FCSTD DOCUMENT
Label: Components Box
objects: Sketcher::SketchObject×4
note: 4 computed .brp shape members not serialized (recipe doc carries the construction recipe); baked Part::Feature solids carry a one-line shape summary decoded from their .brp

FEATURE [Sketcher::SketchObject] Sketch001  label="side, left"
  Placement = pos=(3,0,0) rot=(0,0,1;1.5708rad)
  sketch-geometry (50):
    g0: LineSegment StartX=3 StartY=34.25 StartZ=0 EndX=3 EndY=27.9975 EndZ=0
    g1: LineSegment StartX=3 StartY=27.9975 StartZ=0 EndX=0 EndY=27.9975 EndZ=0
    g2: LineSegment StartX=0 StartY=27.9975 StartZ=0 EndX=0 EndY=21.7475 EndZ=0
    g3: LineSegment StartX=0 StartY=21.7475 StartZ=0 EndX=3 EndY=21.7475 EndZ=0
    g4: LineSegment StartX=3 StartY=21.7475 StartZ=0 EndX=3 EndY=15.4975 EndZ=0
    g5: LineSegment StartX=3 StartY=15.4975 StartZ=0 EndX=0 EndY=15.4975 EndZ=0
    g6: LineSegment StartX=0 StartY=15.4975 StartZ=0 EndX=0 EndY=9.2475 EndZ=0
    g7: LineSegment StartX=0 StartY=9.2475 StartZ=0 EndX=3 EndY=9.2475 EndZ=0
    g8: LineSegment StartX=3 StartY=9.2475 StartZ=0 EndX=3 EndY=0 EndZ=0
    g9: LineSegment StartX=3 StartY=0 StartZ=0 EndX=15.5 EndY=0 EndZ=0
    g10: LineSegment StartX=15.5 StartY=0 StartZ=0 EndX=15.5 EndY=3 EndZ=0
    g11: LineSegment StartX=15.5 StartY=3 StartZ=0 EndX=28 EndY=3 EndZ=0
    g12: LineSegment StartX=28 StartY=3 StartZ=0 EndX=28 EndY=0 EndZ=0
    g13: LineSegment StartX=28 StartY=0 StartZ=0 EndX=40.5 EndY=0 EndZ=0
    g14: LineSegment StartX=40.5 StartY=0 StartZ=0 EndX=40.5 EndY=3 EndZ=0
    g15: LineSegment StartX=40.5 StartY=3 StartZ=0 EndX=53 EndY=3 EndZ=0
    g16: LineSegment StartX=53 StartY=3 StartZ=0 EndX=53 EndY=0 EndZ=0
    g17: LineSegment StartX=53 StartY=0 StartZ=0 EndX=65.5 EndY=0 EndZ=0
    g18: LineSegment StartX=65.5 StartY=0 StartZ=0 EndX=65.5 EndY=3 EndZ=0
    g19: LineSegment StartX=65.5 StartY=3 StartZ=0 EndX=78 EndY=3 EndZ=0
    g20: LineSegment StartX=78 StartY=3 StartZ=0 EndX=78 EndY=0 EndZ=0
    g21: LineSegment StartX=78 StartY=0 StartZ=0 EndX=90.5 EndY=0 EndZ=0
    g22: LineSegment StartX=90.5 StartY=0 StartZ=0 EndX=90.5 EndY=3 EndZ=0
    g23: LineSegment StartX=90.5 StartY=3 StartZ=0 EndX=103 EndY=3 EndZ=0
    g24: LineSegment StartX=103 StartY=3 StartZ=0 EndX=103 EndY=0 EndZ=0
    g25: LineSegment StartX=103 StartY=0 StartZ=0 EndX=115.5 EndY=0 EndZ=0
    g26: LineSegment StartX=115.5 StartY=0 StartZ=0 EndX=115.5 EndY=3 EndZ=0
    g27: LineSegment StartX=115.5 StartY=3 StartZ=0 EndX=128 EndY=3 EndZ=0
    g28: LineSegment StartX=128 StartY=3 StartZ=0 EndX=128 EndY=9.25 EndZ=0
    g29: LineSegment StartX=128 StartY=9.25 StartZ=0 EndX=131 EndY=9.25 EndZ=0
    g30: LineSegment StartX=131 StartY=9.25 StartZ=0 EndX=131 EndY=15.5 EndZ=0
    g31: LineSegment StartX=131 StartY=15.5 StartZ=0 EndX=128 EndY=15.5 EndZ=0
    g32: LineSegment StartX=128 StartY=15.5 StartZ=0 EndX=128 EndY=21.75 EndZ=0
    g33: LineSegment StartX=128 StartY=21.75 StartZ=0 EndX=131 EndY=21.75 EndZ=0
    g34: LineSegment StartX=131 StartY=21.75 StartZ=0 EndX=131 EndY=28 EndZ=0
    g35: LineSegment StartX=131 StartY=28 StartZ=0 EndX=128 EndY=28 EndZ=0
    g36: LineSegment StartX=128 StartY=28 StartZ=0 EndX=128 EndY=34.25 EndZ=0
    g37: LineSegment StartX=128 StartY=34.25 StartZ=0 EndX=99 EndY=34.25 EndZ=0
    g38: LineSegment StartX=99 StartY=34.25 StartZ=0 EndX=99 EndY=18.625 EndZ=0
    g39: LineSegment StartX=99 StartY=18.625 StartZ=0 EndX=96 EndY=18.625 EndZ=0
    g40: LineSegment StartX=96 StartY=18.625 StartZ=0 EndX=96 EndY=34.25 EndZ=0
    g41: LineSegment StartX=96 StartY=34.25 StartZ=0 EndX=67 EndY=34.25 EndZ=0
    g42: LineSegment StartX=67 StartY=34.25 StartZ=0 EndX=67 EndY=18.625 EndZ=0
    g43: LineSegment StartX=67 StartY=18.625 StartZ=0 EndX=64 EndY=18.625 EndZ=0
    g44: LineSegment StartX=64 StartY=18.625 StartZ=0 EndX=64 EndY=34.25 EndZ=0
    g45: LineSegment StartX=64 StartY=34.25 StartZ=0 EndX=35 EndY=34.25 EndZ=0
    g46: LineSegment StartX=35 StartY=34.25 StartZ=0 EndX=35 EndY=18.625 EndZ=0
    g47: LineSegment StartX=35 StartY=18.625 StartZ=0 EndX=32 EndY=18.625 EndZ=0
    g48: LineSegment StartX=32 StartY=18.625 StartZ=0 EndX=32 EndY=34.25 EndZ=0
    g49: LineSegment StartX=32 StartY=34.25 StartZ=0 EndX=3 EndY=34.25 EndZ=0
  constraints (150):
    c: Coincident(g0,g1)
    c: Coincident(g1,g2)
    c: Coincident(g2,g3)
    c: Coincident(g3,g4)
    c: Coincident(g4,g5)
    c: Coincident(g5,g6)
    c: Coincident(g6,g7)
    c: Coincident(g7,g8)
    c: Coincident(g8,g9)
    c: Coincident(g9,g10)
    c: Coincident(g10,g11)
    c: Coincident(g11,g12)
    c: Coincident(g12,g13)
    c: Coincident(g13,g14)
    c: Coincident(g14,g15)
    c: Coincident(g15,g16)
    c: Coincident(g16,g17)
    c: Coincident(g17,g18)
    c: Coincident(g18,g19)
    c: Coincident(g19,g20)
    c: Coincident(g20,g21)
    c: Coincident(g21,g22)
    c: Coincident(g22,g23)
    c: Coincident(g23,g24)
    c: Coincident(g24,g25)
    c: Coincident(g25,g26)
    c: Coincident(g28,g29)
    c: Coincident(g29,g30)
    c: Coincident(g30,g31)
    c: Coincident(g31,g32)
    c: Coincident(g32,g33)
    c: Coincident(g33,g34)
    c: Coincident(g34,g35)
    c: Coincident(g35,g36)
    c: Coincident(g37,g38)
    c: Coincident(g38,g39)
    c: Coincident(g39,g40)
    c: Coincident(g40,g41)
    c: Coincident(g41,g42)
    c: Coincident(g42,g43)
    c: Coincident(g43,g44)
    c: Coincident(g44,g45)
    c: Coincident(g45,g46)
    c: Coincident(g46,g47)
    c: Coincident(g47,g48)
    c: Coincident(g48,g49)
    c: Horizontal(g49)
    c: Vertical(g48)
    c: Horizontal(g47)
    c: Vertical(g46)
    c: Horizontal(g45)
    c: Vertical(g44)
    c: Horizontal(g43)
    c: Vertical(g42)
    c: Horizontal(g41)
    c: Vertical(g40)
    c: Horizontal(g39)
    c: Vertical(g38)
    c: Horizontal(g37)
    c: Vertical(g36)
    c: Horizontal(g35)
    c: Vertical(g34)
    c: Coincident(g27,g28)
    c: Coincident(g27,g26)
    c: Vertical(g32)
    c: Vertical(g30)
    c: Vertical(g28)
    c: Vertical(g26)
    c: Horizontal(g31)
    c: Horizontal(g29)
    c: Horizontal(g27)
    c: Horizontal(g25)
    c: Horizontal(g23)
    c: Horizontal(g21)
    c: Horizontal(g19)
    c: Horizontal(g17)
    c: Horizontal(g15)
    c: Horizontal(g13)
    c: Horizontal(g11)
    c: Horizontal(g9)
    c: Horizontal(g7)
    c: Horizontal(g5)
    c: Horizontal(g1)
    c: Vertical(g24)
    c: Vertical(g22)
    c: Vertical(g20)
    c: Vertical(g18)
    c: Vertical(g16)
    c: Vertical(g14)
    c: Vertical(g12)
    c: Vertical(g10)
    c: Vertical(g8)
    c: Vertical(g6)
    c: Vertical(g4)
    c: Vertical(g2)
    c: Vertical(g0)
    c: Horizontal(g3)
    c: DistanceX(g2,g5) = 0
    c: DistanceY(g12,g9) = 0
    c: DistanceY(g14,g11) = 0
    c: DistanceX(g7,g4) = 0
    c: DistanceX(g0,g3) = 0
    c: DistanceY(g16,g13) = 0
    c: DistanceY(g18,g15) = 0
    c: DistanceY(g20,g17) = 0
    c: DistanceY(g19,g22) = 0
    c: DistanceY(g21,g24) = 0
    c: DistanceX(g28,g31) = 0
    c: DistanceX(g30,g33) = 0
    c: DistanceX(g32,g35) = 0
    c: DistanceY(g37,g40) = 0
    c: DistanceY(g39,g42) = 0
    c: DistanceY(g43,g46) = 0
    c: DistanceY(g41,g44) = 0
    c: DistanceY(g45,g48) = 0
    c: DistanceX(g41,g44) = -3
    c: DistanceX(g40,g37) = 3
    c: DistanceX(g45,g48) = -3
    c: DistanceY(g26,g23) = 0
    c: DistanceY(g26,g25) = -3
    c: DistanceX(g6,g7) = 3
    c: DistanceY(g47,g48) = 15.625
    c: DistanceX(g40,g41) = -29
    c: DistanceX(g44,g45) = -29
    c: DistanceY(g1,g2) = -6.25
    c: DistanceY(g3,g4) = -6.25
    c: DistanceY(g5,g6) = -6.25
    c: Horizontal(g33)
    c: DistanceY(g36,g35) = -6.25
    c: DistanceY(g34,g33) = -6.25
    c: DistanceY(g31,g32) = 6.25
    c: DistanceY(g29,g30) = 6.25
    c: DistanceX(g10,g11) = 12.5
    c: DistanceX(g11,g14) = 12.5
    c: DistanceX(g14,g15) = 12.5
    c: DistanceX(g17,g16) = -12.5
    c: DistanceX(g18,g19) = 12.5
    c: DistanceX(g20,g21) = 12.5
    c: DistanceX(g22,g23) = 12.5
    c: DistanceX(g24,g25) = 12.5
    c: Equal(g27,g9)
    c: Coincident(g37,g36)
    c: Coincident(g49,g0)
    c: DistanceY(g1,g0) = 6.2525
    c: DistanceX(g36,g34) = 3
    c: DistanceX(g36,g37) = -29
    c: DistanceX(g0,g48) = 29
    c: DistanceY(g27,g28) = 6.25
    c: DistanceX(g8) = 3
    c: DistanceY(g8) = 0
FEATURE [Sketcher::SketchObject] Sketch002  label="back"
  Placement = pos=(0,128,0) rot=(0,0,1;0rad)
  sketch-geometry (92):
    g0: LineSegment StartX=-0.05217 StartY=34.2293 StartZ=0 EndX=-0.05217 EndY=27.9793 EndZ=0
    g1: LineSegment StartX=-0.05217 StartY=27.9793 StartZ=0 EndX=2.94783 EndY=27.9793 EndZ=0
    g2: LineSegment StartX=2.94783 StartY=27.9793 StartZ=0 EndX=2.94783 EndY=21.7293 EndZ=0
    g3: LineSegment StartX=2.94783 StartY=21.7293 StartZ=0 EndX=-0.05217 EndY=21.7293 EndZ=0
    g4: LineSegment StartX=-0.05217 StartY=21.7293 StartZ=0 EndX=-0.05217 EndY=15.4793 EndZ=0
    g5: LineSegment StartX=-0.05217 StartY=15.4793 StartZ=0 EndX=2.94783 EndY=15.4793 EndZ=0
    g6: LineSegment StartX=2.94783 StartY=15.4793 StartZ=0 EndX=2.94783 EndY=9.2293 EndZ=0
    g7: LineSegment StartX=2.94783 StartY=9.2293 StartZ=0 EndX=-0.05217 EndY=9.2293 EndZ=0
    g8: LineSegment StartX=-0.05217 StartY=9.2293 StartZ=0 EndX=-0.05217 EndY=-0.020704 EndZ=0
    g9: LineSegment StartX=-0.05217 StartY=34.2293 StartZ=0 EndX=31.9478 EndY=34.2293 EndZ=0
    g10: LineSegment StartX=31.9478 StartY=34.2293 StartZ=0 EndX=31.9478 EndY=18.6043 EndZ=0
    g11: LineSegment StartX=31.9478 StartY=18.6043 StartZ=0 EndX=34.9478 EndY=18.6043 EndZ=0
    g12: LineSegment StartX=34.9478 StartY=18.6043 StartZ=0 EndX=34.9478 EndY=34.2293 EndZ=0
    g13: LineSegment StartX=34.9478 StartY=34.2293 StartZ=0 EndX=63.9478 EndY=34.2293 EndZ=0
    g14: LineSegment StartX=63.9478 StartY=34.2293 StartZ=0 EndX=63.9478 EndY=18.6043 EndZ=0
    g15: LineSegment StartX=63.9478 StartY=18.6043 StartZ=0 EndX=66.9478 EndY=18.6043 EndZ=0
    g16: LineSegment StartX=66.9478 StartY=18.6043 StartZ=0 EndX=66.9478 EndY=34.2293 EndZ=0
    g17: LineSegment StartX=66.9478 StartY=34.2293 StartZ=0 EndX=95.9478 EndY=34.2293 EndZ=0
    g18: LineSegment StartX=95.9478 StartY=34.2293 StartZ=0 EndX=95.9478 EndY=18.6043 EndZ=0
    g19: LineSegment StartX=95.9478 StartY=18.6043 StartZ=0 EndX=98.9478 EndY=18.6043 EndZ=0
    g20: LineSegment StartX=98.9478 StartY=18.6043 StartZ=0 EndX=98.9478 EndY=34.2293 EndZ=0
    g21: LineSegment StartX=98.9478 StartY=34.2293 StartZ=0 EndX=127.948 EndY=34.2293 EndZ=0
    g22: LineSegment StartX=127.948 StartY=34.2293 StartZ=0 EndX=127.948 EndY=18.6043 EndZ=0
    g23: LineSegment StartX=127.948 StartY=18.6043 StartZ=0 EndX=133.948 EndY=18.6043 EndZ=0
    g24: LineSegment StartX=133.948 StartY=18.6043 StartZ=0 EndX=133.948 EndY=34.2293 EndZ=0
    g25: LineSegment StartX=133.948 StartY=34.2293 StartZ=0 EndX=162.948 EndY=34.2293 EndZ=0
    g26: LineSegment StartX=162.948 StartY=34.2293 StartZ=0 EndX=162.948 EndY=18.6043 EndZ=0
    g27: LineSegment StartX=162.948 StartY=18.6043 StartZ=0 EndX=165.948 EndY=18.6043 EndZ=0
    g28: LineSegment StartX=165.948 StartY=18.6043 StartZ=0 EndX=165.948 EndY=34.2293 EndZ=0
    g29: LineSegment StartX=165.948 StartY=34.2293 StartZ=0 EndX=194.948 EndY=34.2293 EndZ=0
    g30: LineSegment StartX=194.948 StartY=34.2293 StartZ=0 EndX=194.948 EndY=18.6043 EndZ=0
    g31: LineSegment StartX=194.948 StartY=18.6043 StartZ=0 EndX=197.948 EndY=18.6043 EndZ=0
    g32: LineSegment StartX=197.948 StartY=18.6043 StartZ=0 EndX=197.948 EndY=34.2293 EndZ=0
    g33: LineSegment StartX=197.948 StartY=34.2293 StartZ=0 EndX=226.948 EndY=34.2293 EndZ=0
    g34: LineSegment StartX=226.948 StartY=34.2293 StartZ=0 EndX=226.948 EndY=18.6043 EndZ=0
    g35: LineSegment StartX=226.948 StartY=18.6043 StartZ=0 EndX=229.948 EndY=18.6043 EndZ=0
    g36: LineSegment StartX=229.948 StartY=18.6043 StartZ=0 EndX=229.948 EndY=34.2293 EndZ=0
    g37: LineSegment StartX=229.948 StartY=34.2293 StartZ=0 EndX=261.948 EndY=34.2293 EndZ=0
    g38: LineSegment StartX=261.948 StartY=34.2293 StartZ=0 EndX=261.948 EndY=27.9793 EndZ=0
    g39: LineSegment StartX=261.948 StartY=27.9793 StartZ=0 EndX=258.948 EndY=27.9793 EndZ=0
    g40: LineSegment StartX=258.948 StartY=27.9793 StartZ=0 EndX=258.948 EndY=21.7293 EndZ=0
    g41: LineSegment StartX=258.948 StartY=21.7293 StartZ=0 EndX=261.948 EndY=21.7293 EndZ=0
    g42: LineSegment StartX=261.948 StartY=21.7293 StartZ=0 EndX=261.948 EndY=15.4793 EndZ=0
    g43: LineSegment StartX=261.948 StartY=15.4793 StartZ=0 EndX=258.948 EndY=15.4793 EndZ=0
    g44: LineSegment StartX=258.948 StartY=15.4793 StartZ=0 EndX=258.948 EndY=9.2293 EndZ=0
    g45: LineSegment StartX=258.948 StartY=9.2293 StartZ=0 EndX=261.948 EndY=9.2293 EndZ=0
    g46: LineSegment StartX=261.948 StartY=9.2293 StartZ=0 EndX=261.948 EndY=-0.020704 EndZ=0
    g47: LineSegment StartX=261.948 StartY=-0.020704 StartZ=0 EndX=249.698 EndY=-0.020704 EndZ=0
    g48: LineSegment StartX=249.698 StartY=-0.020704 StartZ=0 EndX=249.698 EndY=2.9793 EndZ=0
    g49: LineSegment StartX=249.698 StartY=2.9793 StartZ=0 EndX=237.198 EndY=2.9793 EndZ=0
    g50: LineSegment StartX=237.198 StartY=2.9793 StartZ=0 EndX=237.198 EndY=-0.020704 EndZ=0
    g51: LineSegment StartX=237.198 StartY=-0.020704 StartZ=0 EndX=224.698 EndY=-0.020704 EndZ=0
    g52: LineSegment StartX=224.698 StartY=-0.020704 StartZ=0 EndX=224.698 EndY=2.9793 EndZ=0
    g53: LineSegment StartX=224.698 StartY=2.9793 StartZ=0 EndX=212.198 EndY=2.9793 EndZ=0
    g54: LineSegment StartX=212.198 StartY=2.9793 StartZ=0 EndX=212.198 EndY=-0.020704 EndZ=0
    g55: LineSegment StartX=212.198 StartY=-0.020704 StartZ=0 EndX=199.698 EndY=-0.020704 EndZ=0
    g56: LineSegment StartX=199.698 StartY=-0.020704 StartZ=0 EndX=199.698 EndY=2.9793 EndZ=0
    g57: LineSegment StartX=199.698 StartY=2.9793 StartZ=0 EndX=187.198 EndY=2.9793 EndZ=0
    g58: LineSegment StartX=187.198 StartY=2.9793 StartZ=0 EndX=187.198 EndY=-0.020704 EndZ=0
    g59: LineSegment StartX=187.198 StartY=-0.020704 StartZ=0 EndX=174.698 EndY=-0.020704 EndZ=0
    g60: LineSegment StartX=174.698 StartY=-0.020704 StartZ=0 EndX=174.698 EndY=2.9793 EndZ=0
    g61: LineSegment StartX=174.698 StartY=2.9793 StartZ=0 EndX=162.198 EndY=2.9793 EndZ=0
    g62: LineSegment StartX=162.198 StartY=2.9793 StartZ=0 EndX=162.198 EndY=-0.020704 EndZ=0
    g63: LineSegment StartX=162.198 StartY=-0.020704 StartZ=0 EndX=149.698 EndY=-0.020704 EndZ=0
    g64: LineSegment StartX=149.698 StartY=-0.020704 StartZ=0 EndX=149.698 EndY=2.9793 EndZ=0
    g65: LineSegment StartX=149.698 StartY=2.9793 StartZ=0 EndX=137.198 EndY=2.9793 EndZ=0
    g66: LineSegment StartX=137.198 StartY=2.9793 StartZ=0 EndX=137.198 EndY=-0.020704 EndZ=0
    g67: LineSegment StartX=137.198 StartY=-0.020704 StartZ=0 EndX=124.698 EndY=-0.020704 EndZ=0
    g68: LineSegment StartX=124.698 StartY=-0.020704 StartZ=0 EndX=124.698 EndY=2.9793 EndZ=0
    g69: LineSegment StartX=124.698 StartY=2.9793 StartZ=0 EndX=112.198 EndY=2.9793 EndZ=0
    g70: LineSegment StartX=112.198 StartY=2.9793 StartZ=0 EndX=112.198 EndY=-0.020704 EndZ=0
    g71: LineSegment StartX=112.198 StartY=-0.020704 StartZ=0 EndX=99.6978 EndY=-0.020704 EndZ=0
    g72: LineSegment StartX=99.6978 StartY=-0.020704 StartZ=0 EndX=99.6978 EndY=2.9793 EndZ=0
    g73: LineSegment StartX=99.6978 StartY=2.9793 StartZ=0 EndX=87.1978 EndY=2.9793 EndZ=0
    g74: LineSegment StartX=87.1978 StartY=2.9793 StartZ=0 EndX=87.1978 EndY=-0.020704 EndZ=0
    g75: LineSegment StartX=87.1978 StartY=-0.020704 StartZ=0 EndX=74.6978 EndY=-0.020704 EndZ=0
    g76: LineSegment StartX=74.6978 StartY=-0.020704 StartZ=0 EndX=74.6978 EndY=2.9793 EndZ=0
    g77: LineSegment StartX=74.6978 StartY=2.9793 StartZ=0 EndX=62.1978 EndY=2.9793 EndZ=0
    g78: LineSegment StartX=62.1978 StartY=2.9793 StartZ=0 EndX=62.1978 EndY=-0.020704 EndZ=0
    g79: LineSegment StartX=62.1978 StartY=-0.020704 StartZ=0 EndX=49.6978 EndY=-0.020704 EndZ=0
    g80: LineSegment StartX=49.6978 StartY=-0.020704 StartZ=0 EndX=49.6978 EndY=2.9793 EndZ=0
    g81: LineSegment StartX=49.6978 StartY=2.9793 StartZ=0 EndX=37.1978 EndY=2.9793 EndZ=0
    g82: LineSegment StartX=37.1978 StartY=2.9793 StartZ=0 EndX=37.1978 EndY=-0.020704 EndZ=0
    g83: LineSegment StartX=-0.05217 StartY=-0.020704 StartZ=0 EndX=12.1978 EndY=-0.020704 EndZ=0
    g84: LineSegment StartX=12.1978 StartY=-0.020704 StartZ=0 EndX=12.1978 EndY=2.9793 EndZ=0
    g85: LineSegment StartX=12.1978 StartY=2.9793 StartZ=0 EndX=24.6978 EndY=2.9793 EndZ=0
    g86: LineSegment StartX=24.6978 StartY=2.9793 StartZ=0 EndX=24.6978 EndY=-0.020704 EndZ=0
    g87: LineSegment StartX=24.6978 StartY=-0.020704 StartZ=0 EndX=37.1978 EndY=-0.020704 EndZ=0
    g88: Circle CenterX=50.4478 CenterY=26.7293 CenterZ=0 NormalX=0 NormalY=0 NormalZ=1 Radius=1.75
    g89: Circle CenterX=80.4478 CenterY=26.7293 CenterZ=0 NormalX=0 NormalY=0 NormalZ=1 Radius=1.75
    g90: Circle CenterX=181.448 CenterY=26.7293 CenterZ=0 NormalX=0 NormalY=0 NormalZ=1 Radius=1.75
    g91: Circle CenterX=211.448 CenterY=26.7293 CenterZ=0 NormalX=0 NormalY=0 NormalZ=1 Radius=1.75
  constraints (276):
    c: Coincident(g0,g1)
    c: Coincident(g1,g2)
    c: Coincident(g2,g3)
    c: Coincident(g3,g4)
    c: Coincident(g4,g5)
    c: Coincident(g5,g6)
    c: Coincident(g6,g7)
    c: Coincident(g7,g8)
    c: Vertical(g8)
    c: Coincident(g9,g10)
    c: Vertical(g10)
    c: Coincident(g10,g11)
    c: Coincident(g11,g12)
    c: Coincident(g12,g13)
    c: Coincident(g13,g14)
    c: Vertical(g14)
    c: Coincident(g14,g15)
    c: Coincident(g15,g16)
    c: Coincident(g16,g17)
    c: Horizontal(g17)
    c: Coincident(g17,g18)
    c: Vertical(g18)
    c: Coincident(g18,g19)
    c: Horizontal(g19)
    c: Coincident(g19,g20)
    c: Vertical(g20)
    c: Coincident(g20,g21)
    c: Horizontal(g21)
    c: Coincident(g21,g22)
    c: Coincident(g22,g23)
    c: Horizontal(g23)
    c: Coincident(g23,g24)
    c: Vertical(g24)
    c: Coincident(g24,g25)
    c: Coincident(g25,g26)
    c: Coincident(g26,g27)
    c: Horizontal(g27)
    c: Coincident(g27,g28)
    c: Vertical(g28)
    c: Coincident(g28,g29)
    c: Horizontal(g29)
    c: Coincident(g29,g30)
    c: Coincident(g30,g31)
    c: Horizontal(g31)
    c: Coincident(g31,g32)
    c: Vertical(g32)
    c: Coincident(g32,g33)
    c: Coincident(g33,g34)
    c: Vertical(g34)
    c: Coincident(g34,g35)
    c: Coincident(g35,g36)
    c: Coincident(g36,g37)
    c: Coincident(g38,g39)
    c: Coincident(g39,g40)
    c: Coincident(g40,g41)
    c: Coincident(g41,g42)
    c: Coincident(g42,g43)
    c: Coincident(g43,g44)
    c: Coincident(g44,g45)
    c: Coincident(g45,g46)
    c: Coincident(g46,g47)
    c: Coincident(g47,g48)
    c: Coincident(g48,g49)
    c: Horizontal(g49)
    c: Coincident(g49,g50)
    c: Coincident(g50,g51)
    c: Horizontal(g51)
    c: Coincident(g51,g52)
    c: Coincident(g52,g53)
    c: Horizontal(g53)
    c: Coincident(g53,g54)
    c: Coincident(g54,g55)
    c: Coincident(g55,g56)
    c: Vertical(g56)
    c: Coincident(g56,g57)
    c: Horizontal(g57)
    c: Coincident(g57,g58)
    c: Vertical(g58)
    c: Coincident(g58,g59)
    c: Coincident(g59,g60)
    c: Coincident(g60,g61)
    c: Coincident(g61,g62)
    c: Vertical(g62)
    c: Coincident(g62,g63)
    c: Coincident(g63,g64)
    c: Coincident(g64,g65)
    c: Coincident(g65,g66)
    c: Coincident(g66,g67)
    c: Coincident(g67,g68)
    c: Coincident(g68,g69)
    c: Coincident(g69,g70)
    c: Coincident(g70,g71)
    c: Horizontal(g71)
    c: Coincident(g71,g72)
    c: Coincident(g72,g73)
    c: Coincident(g73,g74)
    c: Vertical(g74)
    c: Coincident(g74,g75)
    c: Horizontal(g75)
    c: Coincident(g75,g76)
    c: Vertical(g76)
    c: Coincident(g76,g77)
    c: Horizontal(g77)
    c: Coincident(g77,g78)
    c: Vertical(g78)
    c: Coincident(g78,g79)
    c: Horizontal(g79)
    c: Coincident(g79,g80)
    c: Coincident(g80,g81)
    c: Coincident(g81,g82)
    c: Vertical(g82)
    c: Vertical(g0)
    c: Vertical(g2)
    c: Vertical(g4)
    c: Vertical(g6)
    c: Horizontal(g1)
    c: Horizontal(g3)
    c: Horizontal(g5)
    c: Horizontal(g7)
    c: Horizontal(g9)
    c: Horizontal(g11)
    c: Horizontal(g13)
    c: Horizontal(g15)
    c: Vertical(g12)
    c: Vertical(g16)
    c: Vertical(g22)
    c: Vertical(g26)
    c: Vertical(g30)
    c: Vertical(g36)
    c: Vertical(g38)
    c: Vertical(g40)
    c: Vertical(g42)
    c: Vertical(g44)
    c: Vertical(g46)
    c: Vertical(g48)
    c: Vertical(g50)
    c: Vertical(g52)
    c: Vertical(g54)
    c: Vertical(g60)
    c: Vertical(g64)
    c: Vertical(g66)
    c: Vertical(g68)
    c: Vertical(g70)
    c: Vertical(g72)
    c: Vertical(g80)
    c: Horizontal(g37)
    c: Horizontal(g39)
    c: Horizontal(g41)
    c: Horizontal(g43)
    c: Horizontal(g45)
    c: Horizontal(g47)
    c: Horizontal(g55)
    c: Horizontal(g59)
    c: Horizontal(g61)
    c: Horizontal(g63)
    c: Horizontal(g65)
    c: Horizontal(g67)
    c: Horizontal(g69)
    c: Horizontal(g73)
    c: Horizontal(g81)
    c: Horizontal(g25)
    c: Horizontal(g33)
    c: DistanceY(g9,g12) = 0
    c: DistanceY(g13,g16) = 0
    c: DistanceY(g17,g20) = 0
    c: DistanceY(g21,g24) = 0
    c: DistanceY(g25,g28) = 0
    c: DistanceY(g29,g32) = 0
    c: DistanceY(g36,g33) = 0
    c: Horizontal(g35)
    c: DistanceY(g34,g31) = 0
    c: DistanceY(g30,g27) = 0
    c: DistanceY(g26,g23) = 0
    c: DistanceY(g22,g19) = 0
    c: DistanceY(g18,g15) = 0
    c: DistanceY(g14,g11) = 0
    c: DistanceY(g80,g77) = 0
    c: DistanceY(g73,g76) = 0
    c: DistanceY(g72,g69) = 0
    c: DistanceY(g68,g65) = 0
    c: DistanceY(g64,g61) = 0
    c: DistanceY(g57,g60) = 0
    c: DistanceY(g53,g56) = 0
    c: DistanceY(g49,g52) = 0
    c: DistanceY(g51,g54) = 0
    c: DistanceY(g55,g58) = 0
    c: DistanceY(g59,g62) = 0
    c: DistanceY(g66,g63) = 0
    c: DistanceY(g70,g67) = 0
    c: DistanceY(g74,g71) = 0
    c: DistanceY(g78,g75) = 0
    c: DistanceY(g79,g82) = 0
    c: DistanceY(g47,g50) = 0
    c: DistanceY(g48,g47) = -3
    c: DistanceX(g48,g49) = -12.5
    c: DistanceX(g50,g51) = -12.5
    c: DistanceX(g51,g54) = -12.5
    c: DistanceX(g54,g55) = -12.5
    c: DistanceX(g55,g58) = -12.5
    c: DistanceX(g42,g45) = 0
    c: DistanceX(g43,g40) = 0
    c: DistanceX(g41,g38) = 0
    c: DistanceX(g59,g58) = 12.5
    c: DistanceX(g61,g60) = 12.5
    c: DistanceX(g63,g62) = 12.5
    c: DistanceX(g66,g63) = 12.5
    c: DistanceX(g67,g66) = 12.5
    c: DistanceX(g68,g69) = -12.5
    c: DistanceX(g69,g72) = -12.5
    c: DistanceX(g72,g73) = -12.5
    c: DistanceX(g74,g75) = -12.5
    c: DistanceX(g76,g77) = -12.5
    c: DistanceX(g79,g78) = 12.5
    c: DistanceX(g81,g80) = 12.5
    c: DistanceX(g14,g15) = 3
    c: DistanceX(g18,g19) = 3
    c: DistanceX(g22,g23) = 6
    c: DistanceX(g27,g26) = -3
    c: DistanceX(g30,g31) = 3
    c: DistanceX(g34,g35) = 3
    c: DistanceX(g10,g11) = 3
    c: DistanceX(g13,g12) = -29
    c: DistanceX(g16,g17) = 29
    c: DistanceX(g21,g20) = -29
    c: DistanceX(g24,g25) = 29
    c: DistanceX(g28,g29) = 29
    c: DistanceX(g32,g33) = 29
    c: DistanceX(g7,g4) = 0
    c: DistanceX(g3,g0) = 0
    c: DistanceX(g2,g5) = 0
    c: DistanceX(g7,g6) = 3
    c: DistanceX(g44,g45) = 3
    c: DistanceY(g8,g7) = 9.25
    c: DistanceY(g7,g4) = 6.25
    c: DistanceY(g5,g2) = 6.25
    c: DistanceY(g3,g0) = 6.25
    c: DistanceY(g46,g45) = 9.25
    c: DistanceY(g45,g42) = 6.25
    c: DistanceY(g42,g41) = 6.25
    c: DistanceY(g41,g38) = 6.25
    c: DistanceX(g37,g36) = -32
    c: DistanceY(g10,g9) = 15.625
    c: DistanceX(g8) = -0.05217
    c: DistanceY(g8) = -0.020704
    c: Coincident(g84,g85)
    c: Coincident(g85,g86)
    c: Coincident(g86,g87)
    c: Coincident(g87,g82)
    c: Horizontal(g87)
    c: Horizontal(g85)
    c: Horizontal(g83)
    c: Vertical(g84)
    c: Vertical(g86)
    c: DistanceY(g83,g86) = 0
    c: DistanceY(g85,g81) = 0
    c: Coincident(g83,g8)
    c: DistanceX(g86,g82) = 12.5
    c: DistanceX(g85,g84) = -12.5
    c: Coincident(g84,g83)
    c: Equal(g47,g83)
    c: Coincident(g9,g0)
    c: Coincident(g38,g37)
    c: DistanceY(g37,g38) = -6.25
    c: DistanceX(g9,g0) = -32
    c: Radius(g88) = 1.75
    c: Radius(g89) = 1.75
    c: DistanceY(g89,g88) = 0
    c: DistanceX(g89,g88) = -30
    c: Radius(g91) = 1.75
    c: Radius(g90) = 1.75
    c: DistanceY(g90,g91) = 0
    c: DistanceX(g90,g91) = 30
    c: DistanceY(g90,g29) = 7.5
    c: DistanceY(g89,g17) = 7.5
    c: DistanceX(g89,g15) = -13.5
    c: DistanceX(g90,g30) = 13.5
FEATURE [Sketcher::SketchObject] Sketch003  label="front"
  Placement = pos=(0,3,0) rot=(1,0,0;3.14159rad)
  sketch-geometry (88):
    g0: LineSegment StartX=-0.05217 StartY=34.2293 StartZ=0 EndX=-0.05217 EndY=27.9793 EndZ=0
    g1: LineSegment StartX=-0.05217 StartY=27.9793 StartZ=0 EndX=2.94783 EndY=27.9793 EndZ=0
    g2: LineSegment StartX=2.94783 StartY=27.9793 StartZ=0 EndX=2.94783 EndY=21.7293 EndZ=0
    g3: LineSegment StartX=2.94783 StartY=21.7293 StartZ=0 EndX=-0.05217 EndY=21.7293 EndZ=0
    g4: LineSegment StartX=-0.05217 StartY=21.7293 StartZ=0 EndX=-0.05217 EndY=15.4793 EndZ=0
    g5: LineSegment StartX=-0.05217 StartY=15.4793 StartZ=0 EndX=2.94783 EndY=15.4793 EndZ=0
    g6: LineSegment StartX=2.94783 StartY=15.4793 StartZ=0 EndX=2.94783 EndY=9.2293 EndZ=0
    g7: LineSegment StartX=2.94783 StartY=9.2293 StartZ=0 EndX=-0.05217 EndY=9.2293 EndZ=0
    g8: LineSegment StartX=-0.05217 StartY=9.2293 StartZ=0 EndX=-0.05217 EndY=-0.020704 EndZ=0
    g9: LineSegment StartX=-0.05217 StartY=34.2293 StartZ=0 EndX=31.9478 EndY=34.2293 EndZ=0
    g10: LineSegment StartX=31.9478 StartY=34.2293 StartZ=0 EndX=31.9478 EndY=18.6043 EndZ=0
    g11: LineSegment StartX=31.9478 StartY=18.6043 StartZ=0 EndX=34.9478 EndY=18.6043 EndZ=0
    g12: LineSegment StartX=34.9478 StartY=18.6043 StartZ=0 EndX=34.9478 EndY=34.2293 EndZ=0
    g13: LineSegment StartX=34.9478 StartY=34.2293 StartZ=0 EndX=63.9478 EndY=34.2293 EndZ=0
    g14: LineSegment StartX=63.9478 StartY=34.2293 StartZ=0 EndX=63.9478 EndY=18.6043 EndZ=0
    g15: LineSegment StartX=63.9478 StartY=18.6043 StartZ=0 EndX=66.9478 EndY=18.6043 EndZ=0
    g16: LineSegment StartX=66.9478 StartY=18.6043 StartZ=0 EndX=66.9478 EndY=34.2293 EndZ=0
    g17: LineSegment StartX=66.9478 StartY=34.2293 StartZ=0 EndX=95.9478 EndY=34.2293 EndZ=0
    g18: LineSegment StartX=95.9478 StartY=34.2293 StartZ=0 EndX=95.9478 EndY=18.6043 EndZ=0
    g19: LineSegment StartX=95.9478 StartY=18.6043 StartZ=0 EndX=98.9478 EndY=18.6043 EndZ=0
    g20: LineSegment StartX=98.9478 StartY=18.6043 StartZ=0 EndX=98.9478 EndY=34.2293 EndZ=0
    g21: LineSegment StartX=98.9478 StartY=34.2293 StartZ=0 EndX=127.948 EndY=34.2293 EndZ=0
    g22: LineSegment StartX=127.948 StartY=34.2293 StartZ=0 EndX=127.948 EndY=18.6043 EndZ=0
    g23: LineSegment StartX=127.948 StartY=18.6043 StartZ=0 EndX=133.948 EndY=18.6043 EndZ=0
    g24: LineSegment StartX=133.948 StartY=18.6043 StartZ=0 EndX=133.948 EndY=34.2293 EndZ=0
    g25: LineSegment StartX=133.948 StartY=34.2293 StartZ=0 EndX=162.948 EndY=34.2293 EndZ=0
    g26: LineSegment StartX=162.948 StartY=34.2293 StartZ=0 EndX=162.948 EndY=18.6043 EndZ=0
    g27: LineSegment StartX=162.948 StartY=18.6043 StartZ=0 EndX=165.948 EndY=18.6043 EndZ=0
    g28: LineSegment StartX=165.948 StartY=18.6043 StartZ=0 EndX=165.948 EndY=34.2293 EndZ=0
    g29: LineSegment StartX=165.948 StartY=34.2293 StartZ=0 EndX=194.948 EndY=34.2293 EndZ=0
    g30: LineSegment StartX=194.948 StartY=34.2293 StartZ=0 EndX=194.948 EndY=18.6043 EndZ=0
    g31: LineSegment StartX=194.948 StartY=18.6043 StartZ=0 EndX=197.948 EndY=18.6043 EndZ=0
    g32: LineSegment StartX=197.948 StartY=18.6043 StartZ=0 EndX=197.948 EndY=34.2293 EndZ=0
    g33: LineSegment StartX=197.948 StartY=34.2293 StartZ=0 EndX=226.948 EndY=34.2293 EndZ=0
    g34: LineSegment StartX=226.948 StartY=34.2293 StartZ=0 EndX=226.948 EndY=18.6043 EndZ=0
    g35: LineSegment StartX=226.948 StartY=18.6043 StartZ=0 EndX=229.948 EndY=18.6043 EndZ=0
    g36: LineSegment StartX=229.948 StartY=18.6043 StartZ=0 EndX=229.948 EndY=34.2293 EndZ=0
    g37: LineSegment StartX=229.948 StartY=34.2293 StartZ=0 EndX=261.948 EndY=34.2293 EndZ=0
    g38: LineSegment StartX=261.948 StartY=34.2293 StartZ=0 EndX=261.948 EndY=27.9793 EndZ=0
    g39: LineSegment StartX=261.948 StartY=27.9793 StartZ=0 EndX=258.948 EndY=27.9793 EndZ=0
    g40: LineSegment StartX=258.948 StartY=27.9793 StartZ=0 EndX=258.948 EndY=21.7293 EndZ=0
    g41: LineSegment StartX=258.948 StartY=21.7293 StartZ=0 EndX=261.948 EndY=21.7293 EndZ=0
    g42: LineSegment StartX=261.948 StartY=21.7293 StartZ=0 EndX=261.948 EndY=15.4793 EndZ=0
    g43: LineSegment StartX=261.948 StartY=15.4793 StartZ=0 EndX=258.948 EndY=15.4793 EndZ=0
    g44: LineSegment StartX=258.948 StartY=15.4793 StartZ=0 EndX=258.948 EndY=9.2293 EndZ=0
    g45: LineSegment StartX=258.948 StartY=9.2293 StartZ=0 EndX=261.948 EndY=9.2293 EndZ=0
    g46: LineSegment StartX=261.948 StartY=9.2293 StartZ=0 EndX=261.948 EndY=-0.020704 EndZ=0
    g47: LineSegment StartX=261.948 StartY=-0.020704 StartZ=0 EndX=249.698 EndY=-0.020704 EndZ=0
    g48: LineSegment StartX=249.698 StartY=-0.020704 StartZ=0 EndX=249.698 EndY=2.9793 EndZ=0
    g49: LineSegment StartX=249.698 StartY=2.9793 StartZ=0 EndX=237.198 EndY=2.9793 EndZ=0
    g50: LineSegment StartX=237.198 StartY=2.9793 StartZ=0 EndX=237.198 EndY=-0.020704 EndZ=0
    g51: LineSegment StartX=237.198 StartY=-0.020704 StartZ=0 EndX=224.698 EndY=-0.020704 EndZ=0
    g52: LineSegment StartX=224.698 StartY=-0.020704 StartZ=0 EndX=224.698 EndY=2.9793 EndZ=0
    g53: LineSegment StartX=224.698 StartY=2.9793 StartZ=0 EndX=212.198 EndY=2.9793 EndZ=0
    g54: LineSegment StartX=212.198 StartY=2.9793 StartZ=0 EndX=212.198 EndY=-0.020704 EndZ=0
    g55: LineSegment StartX=212.198 StartY=-0.020704 StartZ=0 EndX=199.698 EndY=-0.020704 EndZ=0
    g56: LineSegment StartX=199.698 StartY=-0.020704 StartZ=0 EndX=199.698 EndY=2.9793 EndZ=0
    g57: LineSegment StartX=199.698 StartY=2.9793 StartZ=0 EndX=187.198 EndY=2.9793 EndZ=0
    g58: LineSegment StartX=187.198 StartY=2.9793 StartZ=0 EndX=187.198 EndY=-0.020704 EndZ=0
    g59: LineSegment StartX=187.198 StartY=-0.020704 StartZ=0 EndX=174.698 EndY=-0.020704 EndZ=0
    g60: LineSegment StartX=174.698 StartY=-0.020704 StartZ=0 EndX=174.698 EndY=2.9793 EndZ=0
    g61: LineSegment StartX=174.698 StartY=2.9793 StartZ=0 EndX=162.198 EndY=2.9793 EndZ=0
    g62: LineSegment StartX=162.198 StartY=2.9793 StartZ=0 EndX=162.198 EndY=-0.020704 EndZ=0
    g63: LineSegment StartX=162.198 StartY=-0.020704 StartZ=0 EndX=149.698 EndY=-0.020704 EndZ=0
    g64: LineSegment StartX=149.698 StartY=-0.020704 StartZ=0 EndX=149.698 EndY=2.9793 EndZ=0
    g65: LineSegment StartX=149.698 StartY=2.9793 StartZ=0 EndX=137.198 EndY=2.9793 EndZ=0
    g66: LineSegment StartX=137.198 StartY=2.9793 StartZ=0 EndX=137.198 EndY=-0.020704 EndZ=0
    g67: LineSegment StartX=137.198 StartY=-0.020704 StartZ=0 EndX=124.698 EndY=-0.020704 EndZ=0
    g68: LineSegment StartX=124.698 StartY=-0.020704 StartZ=0 EndX=124.698 EndY=2.9793 EndZ=0
    g69: LineSegment StartX=124.698 StartY=2.9793 StartZ=0 EndX=112.198 EndY=2.9793 EndZ=0
    g70: LineSegment StartX=112.198 StartY=2.9793 StartZ=0 EndX=112.198 EndY=-0.020704 EndZ=0
    g71: LineSegment StartX=112.198 StartY=-0.020704 StartZ=0 EndX=99.6978 EndY=-0.020704 EndZ=0
    g72: LineSegment StartX=99.6978 StartY=-0.020704 StartZ=0 EndX=99.6978 EndY=2.9793 EndZ=0
    g73: LineSegment StartX=99.6978 StartY=2.9793 StartZ=0 EndX=87.1978 EndY=2.9793 EndZ=0
    g74: LineSegment StartX=87.1978 StartY=2.9793 StartZ=0 EndX=87.1978 EndY=-0.020704 EndZ=0
    g75: LineSegment StartX=87.1978 StartY=-0.020704 StartZ=0 EndX=74.6978 EndY=-0.020704 EndZ=0
    g76: LineSegment StartX=74.6978 StartY=-0.020704 StartZ=0 EndX=74.6978 EndY=2.9793 EndZ=0
    g77: LineSegment StartX=74.6978 StartY=2.9793 StartZ=0 EndX=62.1978 EndY=2.9793 EndZ=0
    g78: LineSegment StartX=62.1978 StartY=2.9793 StartZ=0 EndX=62.1978 EndY=-0.020704 EndZ=0
    g79: LineSegment StartX=62.1978 StartY=-0.020704 StartZ=0 EndX=49.6978 EndY=-0.020704 EndZ=0
    g80: LineSegment StartX=49.6978 StartY=-0.020704 StartZ=0 EndX=49.6978 EndY=2.9793 EndZ=0
    g81: LineSegment StartX=49.6978 StartY=2.9793 StartZ=0 EndX=37.1978 EndY=2.9793 EndZ=0
    g82: LineSegment StartX=37.1978 StartY=2.9793 StartZ=0 EndX=37.1978 EndY=-0.020704 EndZ=0
    g83: LineSegment StartX=-0.05217 StartY=-0.020704 StartZ=0 EndX=12.1978 EndY=-0.020704 EndZ=0
    g84: LineSegment StartX=12.1978 StartY=-0.020704 StartZ=0 EndX=12.1978 EndY=2.9793 EndZ=0
    g85: LineSegment StartX=12.1978 StartY=2.9793 StartZ=0 EndX=24.6978 EndY=2.9793 EndZ=0
    g86: LineSegment StartX=24.6978 StartY=2.9793 StartZ=0 EndX=24.6978 EndY=-0.020704 EndZ=0
    g87: LineSegment StartX=24.6978 StartY=-0.020704 StartZ=0 EndX=37.1978 EndY=-0.020704 EndZ=0
  constraints (264):
    c: Coincident(g0,g1)
    c: Coincident(g1,g2)
    c: Coincident(g2,g3)
    c: Coincident(g3,g4)
    c: Coincident(g4,g5)
    c: Coincident(g5,g6)
    c: Coincident(g6,g7)
    c: Coincident(g7,g8)
    c: Vertical(g8)
    c: Coincident(g9,g10)
    c: Vertical(g10)
    c: Coincident(g10,g11)
    c: Coincident(g11,g12)
    c: Coincident(g12,g13)
    c: Coincident(g13,g14)
    c: Vertical(g14)
    c: Coincident(g14,g15)
    c: Coincident(g15,g16)
    c: Coincident(g16,g17)
    c: Horizontal(g17)
    c: Coincident(g17,g18)
    c: Vertical(g18)
    c: Coincident(g18,g19)
    c: Horizontal(g19)
    c: Coincident(g19,g20)
    c: Vertical(g20)
    c: Coincident(g20,g21)
    c: Horizontal(g21)
    c: Coincident(g21,g22)
    c: Coincident(g22,g23)
    c: Horizontal(g23)
    c: Coincident(g23,g24)
    c: Vertical(g24)
    c: Coincident(g24,g25)
    c: Coincident(g25,g26)
    c: Coincident(g26,g27)
    c: Horizontal(g27)
    c: Coincident(g27,g28)
    c: Vertical(g28)
    c: Coincident(g28,g29)
    c: Horizontal(g29)
    c: Coincident(g29,g30)
    c: Coincident(g30,g31)
    c: Horizontal(g31)
    c: Coincident(g31,g32)
    c: Vertical(g32)
    c: Coincident(g32,g33)
    c: Coincident(g33,g34)
    c: Vertical(g34)
    c: Coincident(g34,g35)
    c: Coincident(g35,g36)
    c: Coincident(g36,g37)
    c: Coincident(g38,g39)
    c: Coincident(g39,g40)
    c: Coincident(g40,g41)
    c: Coincident(g41,g42)
    c: Coincident(g42,g43)
    c: Coincident(g43,g44)
    c: Coincident(g44,g45)
    c: Coincident(g45,g46)
    c: Coincident(g46,g47)
    c: Coincident(g47,g48)
    c: Coincident(g48,g49)
    c: Horizontal(g49)
    c: Coincident(g49,g50)
    c: Coincident(g50,g51)
    c: Horizontal(g51)
    c: Coincident(g51,g52)
    c: Coincident(g52,g53)
    c: Horizontal(g53)
    c: Coincident(g53,g54)
    c: Coincident(g54,g55)
    c: Coincident(g55,g56)
    c: Vertical(g56)
    c: Coincident(g56,g57)
    c: Horizontal(g57)
    c: Coincident(g57,g58)
    c: Vertical(g58)
    c: Coincident(g58,g59)
    c: Coincident(g59,g60)
    c: Coincident(g60,g61)
    c: Coincident(g61,g62)
    c: Vertical(g62)
    c: Coincident(g62,g63)
    c: Coincident(g63,g64)
    c: Coincident(g64,g65)
    c: Coincident(g65,g66)
    c: Coincident(g66,g67)
    c: Coincident(g67,g68)
    c: Coincident(g68,g69)
    c: Coincident(g69,g70)
    c: Coincident(g70,g71)
    c: Horizontal(g71)
    c: Coincident(g71,g72)
    c: Coincident(g72,g73)
    c: Coincident(g73,g74)
    c: Vertical(g74)
    c: Coincident(g74,g75)
    c: Horizontal(g75)
    c: Coincident(g75,g76)
    c: Vertical(g76)
    c: Coincident(g76,g77)
    c: Horizontal(g77)
    c: Coincident(g77,g78)
    c: Vertical(g78)
    c: Coincident(g78,g79)
    c: Horizontal(g79)
    c: Coincident(g79,g80)
    c: Coincident(g80,g81)
    c: Coincident(g81,g82)
    c: Vertical(g82)
    c: Vertical(g0)
    c: Vertical(g2)
    c: Vertical(g4)
    c: Vertical(g6)
    c: Horizontal(g1)
    c: Horizontal(g3)
    c: Horizontal(g5)
    c: Horizontal(g7)
    c: Horizontal(g9)
    c: Horizontal(g11)
    c: Horizontal(g13)
    c: Horizontal(g15)
    c: Vertical(g12)
    c: Vertical(g16)
    c: Vertical(g22)
    c: Vertical(g26)
    c: Vertical(g30)
    c: Vertical(g36)
    c: Vertical(g38)
    c: Vertical(g40)
    c: Vertical(g42)
    c: Vertical(g44)
    c: Vertical(g46)
    c: Vertical(g48)
    c: Vertical(g50)
    c: Vertical(g52)
    c: Vertical(g54)
    c: Vertical(g60)
    c: Vertical(g64)
    c: Vertical(g66)
    c: Vertical(g68)
    c: Vertical(g70)
    c: Vertical(g72)
    c: Vertical(g80)
    c: Horizontal(g37)
    c: Horizontal(g39)
    c: Horizontal(g41)
    c: Horizontal(g43)
    c: Horizontal(g45)
    c: Horizontal(g47)
    c: Horizontal(g55)
    c: Horizontal(g59)
    c: Horizontal(g61)
    c: Horizontal(g63)
    c: Horizontal(g65)
    c: Horizontal(g67)
    c: Horizontal(g69)
    c: Horizontal(g73)
    c: Horizontal(g81)
    c: Horizontal(g25)
    c: Horizontal(g33)
    c: DistanceY(g9,g12) = 0
    c: DistanceY(g13,g16) = 0
    c: DistanceY(g17,g20) = 0
    c: DistanceY(g21,g24) = 0
    c: DistanceY(g25,g28) = 0
    c: DistanceY(g29,g32) = 0
    c: DistanceY(g36,g33) = 0
    c: Horizontal(g35)
    c: DistanceY(g34,g31) = 0
    c: DistanceY(g30,g27) = 0
    c: DistanceY(g26,g23) = 0
    c: DistanceY(g22,g19) = 0
    c: DistanceY(g18,g15) = 0
    c: DistanceY(g14,g11) = 0
    c: DistanceY(g80,g77) = 0
    c: DistanceY(g73,g76) = 0
    c: DistanceY(g72,g69) = 0
    c: DistanceY(g68,g65) = 0
    c: DistanceY(g64,g61) = 0
    c: DistanceY(g57,g60) = 0
    c: DistanceY(g53,g56) = 0
    c: DistanceY(g49,g52) = 0
    c: DistanceY(g51,g54) = 0
    c: DistanceY(g55,g58) = 0
    c: DistanceY(g59,g62) = 0
    c: DistanceY(g66,g63) = 0
    c: DistanceY(g70,g67) = 0
    c: DistanceY(g74,g71) = 0
    c: DistanceY(g78,g75) = 0
    c: DistanceY(g79,g82) = 0
    c: DistanceY(g47,g50) = 0
    c: DistanceY(g48,g47) = -3
    c: DistanceX(g48,g49) = -12.5
    c: DistanceX(g50,g51) = -12.5
    c: DistanceX(g51,g54) = -12.5
    c: DistanceX(g54,g55) = -12.5
    c: DistanceX(g55,g58) = -12.5
    c: DistanceX(g42,g45) = 0
    c: DistanceX(g43,g40) = 0
    c: DistanceX(g41,g38) = 0
    c: DistanceX(g59,g58) = 12.5
    c: DistanceX(g61,g60) = 12.5
    c: DistanceX(g63,g62) = 12.5
    c: DistanceX(g66,g63) = 12.5
    c: DistanceX(g67,g66) = 12.5
    c: DistanceX(g68,g69) = -12.5
    c: DistanceX(g69,g72) = -12.5
    c: DistanceX(g72,g73) = -12.5
    c: DistanceX(g74,g75) = -12.5
    c: DistanceX(g76,g77) = -12.5
    c: DistanceX(g79,g78) = 12.5
    c: DistanceX(g81,g80) = 12.5
    c: DistanceX(g14,g15) = 3
    c: DistanceX(g18,g19) = 3
    c: DistanceX(g22,g23) = 6
    c: DistanceX(g27,g26) = -3
    c: DistanceX(g30,g31) = 3
    c: DistanceX(g34,g35) = 3
    c: DistanceX(g10,g11) = 3
    c: DistanceX(g13,g12) = -29
    c: DistanceX(g16,g17) = 29
    c: DistanceX(g21,g20) = -29
    c: DistanceX(g24,g25) = 29
    c: DistanceX(g28,g29) = 29
    c: DistanceX(g32,g33) = 29
    c: DistanceX(g7,g4) = 0
    c: DistanceX(g3,g0) = 0
    c: DistanceX(g2,g5) = 0
    c: DistanceX(g7,g6) = 3
    c: DistanceX(g44,g45) = 3
    c: DistanceY(g8,g7) = 9.25
    c: DistanceY(g7,g4) = 6.25
    c: DistanceY(g5,g2) = 6.25
    c: DistanceY(g3,g0) = 6.25
    c: DistanceY(g46,g45) = 9.25
    c: DistanceY(g45,g42) = 6.25
    c: DistanceY(g42,g41) = 6.25
    c: DistanceY(g41,g38) = 6.25
    c: DistanceX(g37,g36) = -32
    c: DistanceY(g10,g9) = 15.625
    c: DistanceX(g8) = -0.05217
    c: DistanceY(g8) = -0.020704
    c: Coincident(g84,g85)
    c: Coincident(g85,g86)
    c: Coincident(g86,g87)
    c: Coincident(g87,g82)
    c: Horizontal(g87)
    c: Horizontal(g85)
    c: Horizontal(g83)
    c: Vertical(g84)
    c: Vertical(g86)
    c: DistanceY(g83,g86) = 0
    c: DistanceY(g85,g81) = 0
    c: Coincident(g83,g8)
    c: DistanceX(g86,g82) = 12.5
    c: DistanceX(g85,g84) = -12.5
    c: Coincident(g84,g83)
    c: Equal(g47,g83)
    c: Coincident(g9,g0)
    c: Coincident(g38,g37)
    c: DistanceY(g37,g38) = -6.25
    c: DistanceX(g9,g0) = -32
FEATURE [Sketcher::SketchObject] Sketch004  label="side, right"
  Placement = pos=(259,0,0) rot=(0.707107,0.707107,0;3.14159rad)
  sketch-geometry (50):
    g0: LineSegment StartX=3 StartY=34.25 StartZ=0 EndX=3 EndY=27.9975 EndZ=0
    g1: LineSegment StartX=3 StartY=27.9975 StartZ=0 EndX=0 EndY=27.9975 EndZ=0
    g2: LineSegment StartX=0 StartY=27.9975 StartZ=0 EndX=0 EndY=21.7475 EndZ=0
    g3: LineSegment StartX=0 StartY=21.7475 StartZ=0 EndX=3 EndY=21.7475 EndZ=0
    g4: LineSegment StartX=3 StartY=21.7475 StartZ=0 EndX=3 EndY=15.4975 EndZ=0
    g5: LineSegment StartX=3 StartY=15.4975 StartZ=0 EndX=0 EndY=15.4975 EndZ=0
    g6: LineSegment StartX=0 StartY=15.4975 StartZ=0 EndX=0 EndY=9.2475 EndZ=0
    g7: LineSegment StartX=0 StartY=9.2475 StartZ=0 EndX=3 EndY=9.2475 EndZ=0
    g8: LineSegment StartX=3 StartY=9.2475 StartZ=0 EndX=3 EndY=0 EndZ=0
    g9: LineSegment StartX=3 StartY=0 StartZ=0 EndX=15.5 EndY=0 EndZ=0
    g10: LineSegment StartX=15.5 StartY=0 StartZ=0 EndX=15.5 EndY=3 EndZ=0
    g11: LineSegment StartX=15.5 StartY=3 StartZ=0 EndX=28 EndY=3 EndZ=0
    g12: LineSegment StartX=28 StartY=3 StartZ=0 EndX=28 EndY=0 EndZ=0
    g13: LineSegment StartX=28 StartY=0 StartZ=0 EndX=40.5 EndY=0 EndZ=0
    g14: LineSegment StartX=40.5 StartY=0 StartZ=0 EndX=40.5 EndY=3 EndZ=0
    g15: LineSegment StartX=40.5 StartY=3 StartZ=0 EndX=53 EndY=3 EndZ=0
    g16: LineSegment StartX=53 StartY=3 StartZ=0 EndX=53 EndY=0 EndZ=0
    g17: LineSegment StartX=53 StartY=0 StartZ=0 EndX=65.5 EndY=0 EndZ=0
    g18: LineSegment StartX=65.5 StartY=0 StartZ=0 EndX=65.5 EndY=3 EndZ=0
    g19: LineSegment StartX=65.5 StartY=3 StartZ=0 EndX=78 EndY=3 EndZ=0
    g20: LineSegment StartX=78 StartY=3 StartZ=0 EndX=78 EndY=0 EndZ=0
    g21: LineSegment StartX=78 StartY=0 StartZ=0 EndX=90.5 EndY=0 EndZ=0
    g22: LineSegment StartX=90.5 StartY=0 StartZ=0 EndX=90.5 EndY=3 EndZ=0
    g23: LineSegment StartX=90.5 StartY=3 StartZ=0 EndX=103 EndY=3 EndZ=0
    g24: LineSegment StartX=103 StartY=3 StartZ=0 EndX=103 EndY=0 EndZ=0
    g25: LineSegment StartX=103 StartY=0 StartZ=0 EndX=115.5 EndY=0 EndZ=0
    g26: LineSegment StartX=115.5 StartY=0 StartZ=0 EndX=115.5 EndY=3 EndZ=0
    g27: LineSegment StartX=115.5 StartY=3 StartZ=0 EndX=128 EndY=3 EndZ=0
    g28: LineSegment StartX=128 StartY=3 StartZ=0 EndX=128 EndY=9.25 EndZ=0
    g29: LineSegment StartX=128 StartY=9.25 StartZ=0 EndX=131 EndY=9.25 EndZ=0
    g30: LineSegment StartX=131 StartY=9.25 StartZ=0 EndX=131 EndY=15.5 EndZ=0
    g31: LineSegment StartX=131 StartY=15.5 StartZ=0 EndX=128 EndY=15.5 EndZ=0
    g32: LineSegment StartX=128 StartY=15.5 StartZ=0 EndX=128 EndY=21.75 EndZ=0
    g33: LineSegment StartX=128 StartY=21.75 StartZ=0 EndX=131 EndY=21.75 EndZ=0
    g34: LineSegment StartX=131 StartY=21.75 StartZ=0 EndX=131 EndY=28 EndZ=0
    g35: LineSegment StartX=131 StartY=28 StartZ=0 EndX=128 EndY=28 EndZ=0
    g36: LineSegment StartX=128 StartY=28 StartZ=0 EndX=128 EndY=34.25 EndZ=0
    g37: LineSegment StartX=128 StartY=34.25 StartZ=0 EndX=99 EndY=34.25 EndZ=0
    g38: LineSegment StartX=99 StartY=34.25 StartZ=0 EndX=99 EndY=18.625 EndZ=0
    g39: LineSegment StartX=99 StartY=18.625 StartZ=0 EndX=96 EndY=18.625 EndZ=0
    g40: LineSegment StartX=96 StartY=18.625 StartZ=0 EndX=96 EndY=34.25 EndZ=0
    g41: LineSegment StartX=96 StartY=34.25 StartZ=0 EndX=67 EndY=34.25 EndZ=0
    g42: LineSegment StartX=67 StartY=34.25 StartZ=0 EndX=67 EndY=18.625 EndZ=0
    g43: LineSegment StartX=67 StartY=18.625 StartZ=0 EndX=64 EndY=18.625 EndZ=0
    g44: LineSegment StartX=64 StartY=18.625 StartZ=0 EndX=64 EndY=34.25 EndZ=0
    g45: LineSegment StartX=64 StartY=34.25 StartZ=0 EndX=35 EndY=34.25 EndZ=0
    g46: LineSegment StartX=35 StartY=34.25 StartZ=0 EndX=35 EndY=18.625 EndZ=0
    g47: LineSegment StartX=35 StartY=18.625 StartZ=0 EndX=32 EndY=18.625 EndZ=0
    g48: LineSegment StartX=32 StartY=18.625 StartZ=0 EndX=32 EndY=34.25 EndZ=0
    g49: LineSegment StartX=32 StartY=34.25 StartZ=0 EndX=3 EndY=34.25 EndZ=0
  constraints (150):
    c: Coincident(g0,g1)
    c: Coincident(g1,g2)
    c: Coincident(g2,g3)
    c: Coincident(g3,g4)
    c: Coincident(g4,g5)
    c: Coincident(g5,g6)
    c: Coincident(g6,g7)
    c: Coincident(g7,g8)
    c: Coincident(g8,g9)
    c: Coincident(g9,g10)
    c: Coincident(g10,g11)
    c: Coincident(g11,g12)
    c: Coincident(g12,g13)
    c: Coincident(g13,g14)
    c: Coincident(g14,g15)
    c: Coincident(g15,g16)
    c: Coincident(g16,g17)
    c: Coincident(g17,g18)
    c: Coincident(g18,g19)
    c: Coincident(g19,g20)
    c: Coincident(g20,g21)
    c: Coincident(g21,g22)
    c: Coincident(g22,g23)
    c: Coincident(g23,g24)
    c: Coincident(g24,g25)
    c: Coincident(g25,g26)
    c: Coincident(g28,g29)
    c: Coincident(g29,g30)
    c: Coincident(g30,g31)
    c: Coincident(g31,g32)
    c: Coincident(g32,g33)
    c: Coincident(g33,g34)
    c: Coincident(g34,g35)
    c: Coincident(g35,g36)
    c: Coincident(g37,g38)
    c: Coincident(g38,g39)
    c: Coincident(g39,g40)
    c: Coincident(g40,g41)
    c: Coincident(g41,g42)
    c: Coincident(g42,g43)
    c: Coincident(g43,g44)
    c: Coincident(g44,g45)
    c: Coincident(g45,g46)
    c: Coincident(g46,g47)
    c: Coincident(g47,g48)
    c: Coincident(g48,g49)
    c: Horizontal(g49)
    c: Vertical(g48)
    c: Horizontal(g47)
    c: Vertical(g46)
    c: Horizontal(g45)
    c: Vertical(g44)
    c: Horizontal(g43)
    c: Vertical(g42)
    c: Horizontal(g41)
    c: Vertical(g40)
    c: Horizontal(g39)
    c: Vertical(g38)
    c: Horizontal(g37)
    c: Vertical(g36)
    c: Horizontal(g35)
    c: Vertical(g34)
    c: Coincident(g27,g28)
    c: Coincident(g27,g26)
    c: Vertical(g32)
    c: Vertical(g30)
    c: Vertical(g28)
    c: Vertical(g26)
    c: Horizontal(g31)
    c: Horizontal(g29)
    c: Horizontal(g27)
    c: Horizontal(g25)
    c: Horizontal(g23)
    c: Horizontal(g21)
    c: Horizontal(g19)
    c: Horizontal(g17)
    c: Horizontal(g15)
    c: Horizontal(g13)
    c: Horizontal(g11)
    c: Horizontal(g9)
    c: Horizontal(g7)
    c: Horizontal(g5)
    c: Horizontal(g1)
    c: Vertical(g24)
    c: Vertical(g22)
    c: Vertical(g20)
    c: Vertical(g18)
    c: Vertical(g16)
    c: Vertical(g14)
    c: Vertical(g12)
    c: Vertical(g10)
    c: Vertical(g8)
    c: Vertical(g6)
    c: Vertical(g4)
    c: Vertical(g2)
    c: Vertical(g0)
    c: Horizontal(g3)
    c: DistanceX(g2,g5) = 0
    c: DistanceY(g12,g9) = 0
    c: DistanceY(g14,g11) = 0
    c: DistanceX(g7,g4) = 0
    c: DistanceX(g0,g3) = 0
    c: DistanceY(g16,g13) = 0
    c: DistanceY(g18,g15) = 0
    c: DistanceY(g20,g17) = 0
    c: DistanceY(g19,g22) = 0
    c: DistanceY(g21,g24) = 0
    c: DistanceX(g28,g31) = 0
    c: DistanceX(g30,g33) = 0
    c: DistanceX(g32,g35) = 0
    c: DistanceY(g37,g40) = 0
    c: DistanceY(g39,g42) = 0
    c: DistanceY(g43,g46) = 0
    c: DistanceY(g41,g44) = 0
    c: DistanceY(g45,g48) = 0
    c: DistanceX(g41,g44) = -3
    c: DistanceX(g40,g37) = 3
    c: DistanceX(g45,g48) = -3
    c: DistanceY(g26,g23) = 0
    c: DistanceY(g26,g25) = -3
    c: DistanceX(g6,g7) = 3
    c: DistanceY(g47,g48) = 15.625
    c: DistanceX(g40,g41) = -29
    c: DistanceX(g44,g45) = -29
    c: DistanceY(g1,g2) = -6.25
    c: DistanceY(g3,g4) = -6.25
    c: DistanceY(g5,g6) = -6.25
    c: Horizontal(g33)
    c: DistanceY(g36,g35) = -6.25
    c: DistanceY(g34,g33) = -6.25
    c: DistanceY(g31,g32) = 6.25
    c: DistanceY(g29,g30) = 6.25
    c: DistanceX(g10,g11) = 12.5
    c: DistanceX(g11,g14) = 12.5
    c: DistanceX(g14,g15) = 12.5
    c: DistanceX(g17,g16) = -12.5
    c: DistanceX(g18,g19) = 12.5
    c: DistanceX(g20,g21) = 12.5
    c: DistanceX(g22,g23) = 12.5
    c: DistanceX(g24,g25) = 12.5
    c: Equal(g27,g9)
    c: Coincident(g37,g36)
    c: Coincident(g49,g0)
    c: DistanceY(g1,g0) = 6.2525
    c: DistanceX(g36,g34) = 3
    c: DistanceX(g36,g37) = -29
    c: DistanceX(g0,g48) = 29
    c: DistanceY(g27,g28) = 6.25
    c: DistanceX(g8) = 3
    c: DistanceY(g8) = 0
